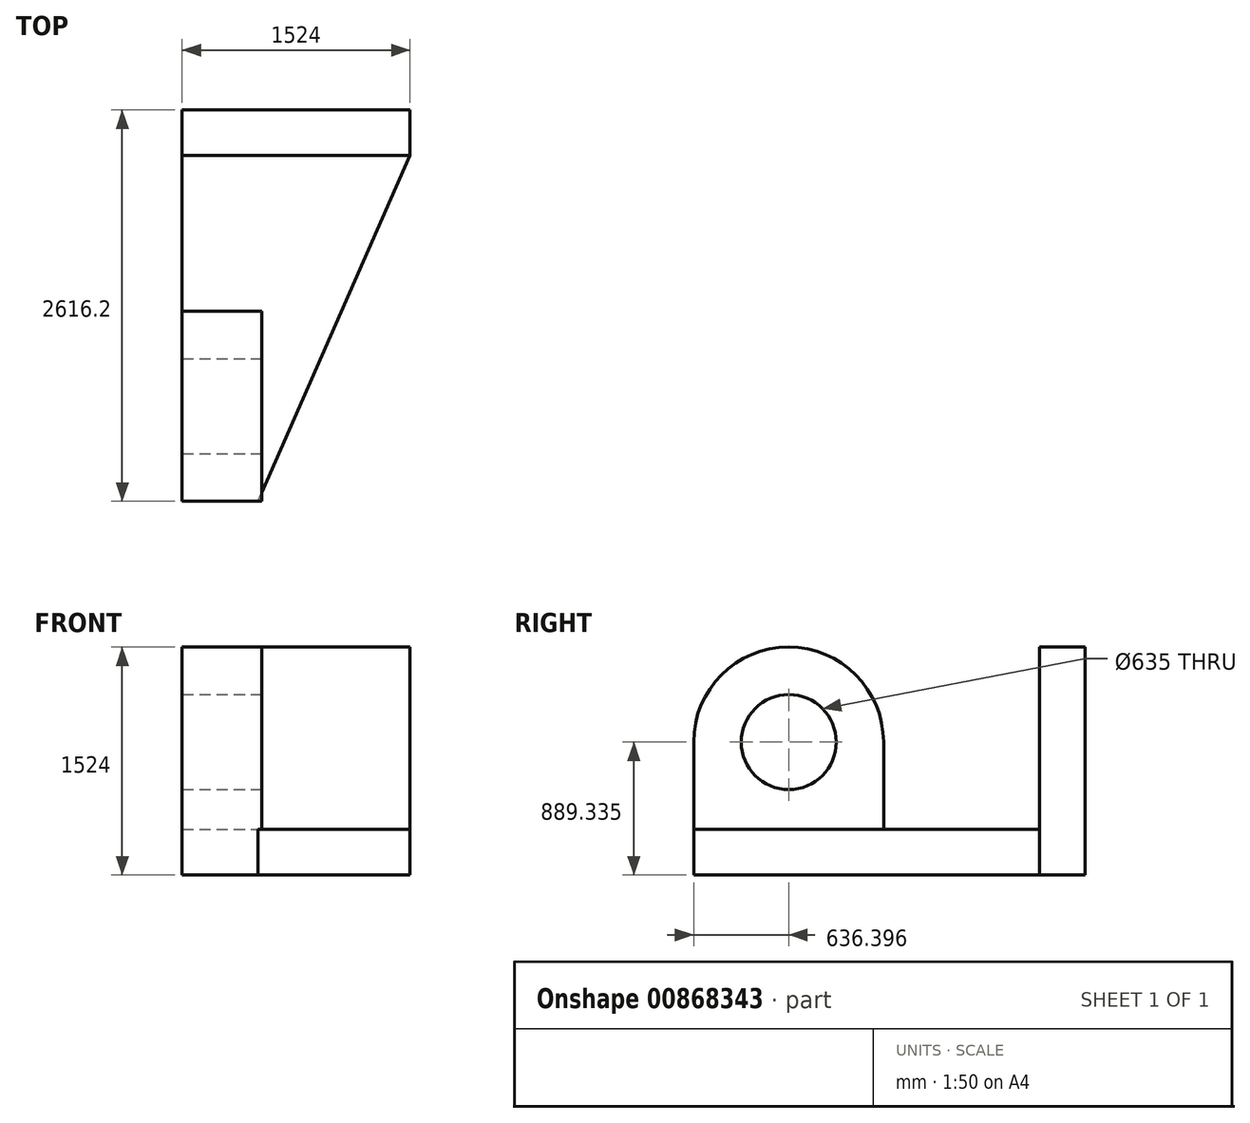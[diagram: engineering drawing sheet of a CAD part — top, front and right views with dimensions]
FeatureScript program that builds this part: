
annotation { "Feature Type Name" : "Feature", "Feature Type Description" : "" }
export const myFeature = defineFeature(function(context is Context, id is Id, definition is map)
    precondition{}
    {
        {
            var Q0;
            Q0=qCreatedBy(makeId("Front.planeOp"),FACE);
            var sketch = newSketch(context, id + "F0", { "sketchPlane" : qUnion([Q0])});
            skLineSegment(sketch, "E0.bottom", {"start": v(0, 0) * mm, "end": v(-1524, 0) * mm});
            skLineSegment(sketch, "E0.top", {"start": v(0, 1524) * mm, "end": v(-1524, 1524) * mm});
            skLineSegment(sketch, "E0.left", {"start": v(0, 0) * mm, "end": v(0, 1524) * mm});
            skLineSegment(sketch, "E0.right", {"start": v(-1524, 0) * mm, "end": v(-1524, 1524) * mm});
            skSolve(sketch);
        }
        {
            var Q0;
            Q0 = qSketchRegion(id + "F0", true);
            var Q1;
            Q1=makeQuery(id+"F0.imprint","IMPRINT",FACE,{"disambiguationData":[TD([[makeQuery(id+"F0.imprint","IMPRINT",EDGE,{"derivedFrom":sQuery(id+"F0.wireOp",EDGE,"E0.bottom")}),-1.0]])]});
            extrude(context, id + "F1", {"entities" : qUnion([Q0, Q1]), "depth" : 304.8 * mm, "offsetDistance" : 25.4 * mm});
        }
        {
            var Q0;
            Q0=makeQuery(id+"F1.opExtrude","SWEPT_FACE",FACE,{"disambiguationData":[OSD([sQuery(id+"F0.wireOp",EDGE,"E0.right")])]});
            var sketch = newSketch(context, id + "F2", { "sketchPlane" : qUnion([Q0])});
            skLineSegment(sketch, "E1", {"start": v(0, 0) * mm, "end": v(0, 304.8) * mm});
            skLineSegment(sketch, "E2", {"start": v(0, 304.8) * mm, "end": v(2616.2, 304.8) * mm});
            skLineSegment(sketch, "E3", {"start": v(2616.2, 304.8) * mm, "end": v(2616.2, 0) * mm});
            skLineSegment(sketch, "E4", {"start": v(2616.2, 0) * mm, "end": v(304.8, 0) * mm});
            skLineSegment(sketch, "E5", {"start": v(304.8, 0) * mm, "end": v(0, 0) * mm});
            skSolve(sketch);
        }
        {
            var Q0;
            {var subQ0=sQuery(id+"F2.wireOp",EDGE,"E3");Q0=makeQuery(id+"F2.imprint","IMPRINT",FACE,{"disambiguationData":[TD([[makeQuery(id+"F2.imprint","IMPRINT",EDGE,{"derivedFrom":subQ0}),-1.0]])]});}
            extrude(context, id + "F3", {"entities" : qUnion([Q0]), "operationType" : NewBodyOperationType.ADD, "oppositeDirection" : true, "depth" : 1524 * mm, "offsetDistance" : 25.4 * mm});
        }
        {
            var Q0;
            Q0=makeQuery(id+"F3.opExtrude","SWEPT_FACE",FACE,{"disambiguationData":[OSD([sQuery(id+"F2.wireOp",EDGE,"E2")])]});
            var sketch = newSketch(context, id + "F4", { "sketchPlane" : qUnion([Q0])});
            skLineSegment(sketch, "E6", {"start": v(-1524, -2616.2) * mm, "end": v(-1016, -2616.2) * mm});
            skLineSegment(sketch, "E7", {"start": v(-1016, -2616.2) * mm, "end": v(0, -304.8) * mm});
            skSolve(sketch);
        }
        {
            var Q0;
            {var subQ0=sQuery(id+"F4.wireOp",EDGE,"E7");Q0=makeQuery(id+"F4.imprint","IMPRINT",FACE,{"disambiguationData":[TD([[makeQuery(id+"F4.imprint","IMPRINT",EDGE,{"derivedFrom":subQ0}),-1.0]])]});}
            extrude(context, id + "F5", {"entities" : qUnion([Q0]), "operationType" : NewBodyOperationType.REMOVE, "oppositeDirection" : true, "depth" : 1008.38 * mm, "offsetDistance" : 25.4 * mm});
        }
        {
            var Q0;
            Q0=makeQuery(id+"F3.opExtrude","SWEPT_FACE",FACE,{"disambiguationData":[OSD([sQuery(id+"F2.wireOp",EDGE,"E2")])]});
            var sketch = newSketch(context, id + "F6", { "sketchPlane" : qUnion([Q0])});
            skLineSegment(sketch, "E8", {"start": v(-1524, -2616.2) * mm, "end": v(-1524, -1346.2) * mm});
            skLineSegment(sketch, "E9", {"start": v(-1524, -1346.2) * mm, "end": v(-1016, -1346.2) * mm});
            skLineSegment(sketch, "E10", {"start": v(-1016, -1346.2) * mm, "end": v(-1016, -2616.2) * mm});
            skSolve(sketch);
        }
        {
            var Q0;
            Q0=makeQuery(id+"F6.imprint","IMPRINT",FACE,{"disambiguationData":[TD([[makeQuery(id+"F6.imprint","IMPRINT",EDGE,{"derivedFrom":sQuery(id+"F6.wireOp",EDGE,"E8")}),1.0]])]});
            extrude(context, id + "F7", {"entities" : qUnion([Q0]), "operationType" : NewBodyOperationType.ADD, "depth" : 1524 * mm, "offsetDistance" : 25.4 * mm});
        }
        {
            var Q0;
            Q0=makeQuery(id+"F7.opExtrude","SWEPT_FACE",FACE,{"disambiguationData":[OSD([sQuery(id+"F6.wireOp",EDGE,"E10")])]});
            extrude(context, id + "F8", {"entities" : qUnion([Q0]), "operationType" : NewBodyOperationType.ADD, "depth" : 25.4 * mm, "offsetDistance" : 25.4 * mm});
        }
        {
            var Q0;
            Q0=makeQuery(id+"F8.opExtrude","CAP_FACE",FACE,{"disambiguationData":[OSD([sQuery(id+"F6.wireOp",EDGE,"E10")])],"isStart":false});
            var sketch = newSketch(context, id + "F9", { "sketchPlane" : qUnion([Q0])});
            skLineSegment(sketch, "E11", {"start": v(-1346.2, 304.8) * mm, "end": v(-1346.2, 889) * mm});
            skLineSegment(sketch, "E12", {"start": v(-1346.2, 889) * mm, "end": v(-1981.2, 889) * mm});
            skLineSegment(sketch, "E13", {"start": v(-1981.2, 889) * mm, "end": v(-1981.2, 1524) * mm});
            skArc(sketch, "E14", {"start": v(-1346.2, 889) * mm, "mid": v(-1981.2, 1524) * mm, "end": v(-2616.2, 889) * mm});
            skSolve(sketch);
        }
        {
            var Q0;
            {var subQ3=sQuery(id+"F9.wireOp",EDGE,"E11");Q0=makeQuery(id+"F9.imprint","IMPRINT",FACE,{"disambiguationData":[TD([[makeQuery(id+"F9.imprint","IMPRINT",EDGE,{"derivedFrom":subQ3}),-1.0]])]});}
            var sketch = newSketch(context, id + "F10", { "sketchPlane" : qUnion([Q0])});
            skCircle(sketch, "E15", {"center": v(-1979.8, 889.33) * mm, "radius": 317.5 * mm});
            skSolve(sketch);
        }
        {
            var Q0;
            Q0=makeQuery(id+"F10.imprint","IMPRINT",FACE,{"disambiguationData":[TD([[makeQuery(id+"F10.imprint","IMPRINT",EDGE,{"derivedFrom":sQuery(id+"F10.wireOp",EDGE,"E15")}),1.0]])]});
            extrude(context, id + "F11", {"entities" : qUnion([Q0]), "operationType" : NewBodyOperationType.REMOVE, "oppositeDirection" : true, "depth" : 1397 * mm, "offsetDistance" : 25.4 * mm});
        }
        {
            var Q0;
            {var subQ0=sQuery(id+"F6.wireOp",EDGE,"E10");var subQ1=makeQuery(id+"F8.opExtrude","CAP_EDGE",EDGE,{"disambiguationData":[OSD([subQ0]),TDD([makeQuery(id+"F7.opExtrude","CAP_EDGE",EDGE,{"disambiguationData":[OSD([subQ0])],"isStart":false})])],"isStart":false});Q0=makeQuery(id+"F9.imprint","IMPRINT",FACE,{"disambiguationData":[TD([[makeQuery(id+"F9.imprint","IMPRINT",EDGE,{"derivedFrom":subQ1}),1.0]])]});}
            extrude(context, id + "F12", {"entities" : qUnion([Q0]), "operationType" : NewBodyOperationType.REMOVE, "oppositeDirection" : true, "depth" : 782.32 * mm, "offsetDistance" : 25.4 * mm});
        }
    });
